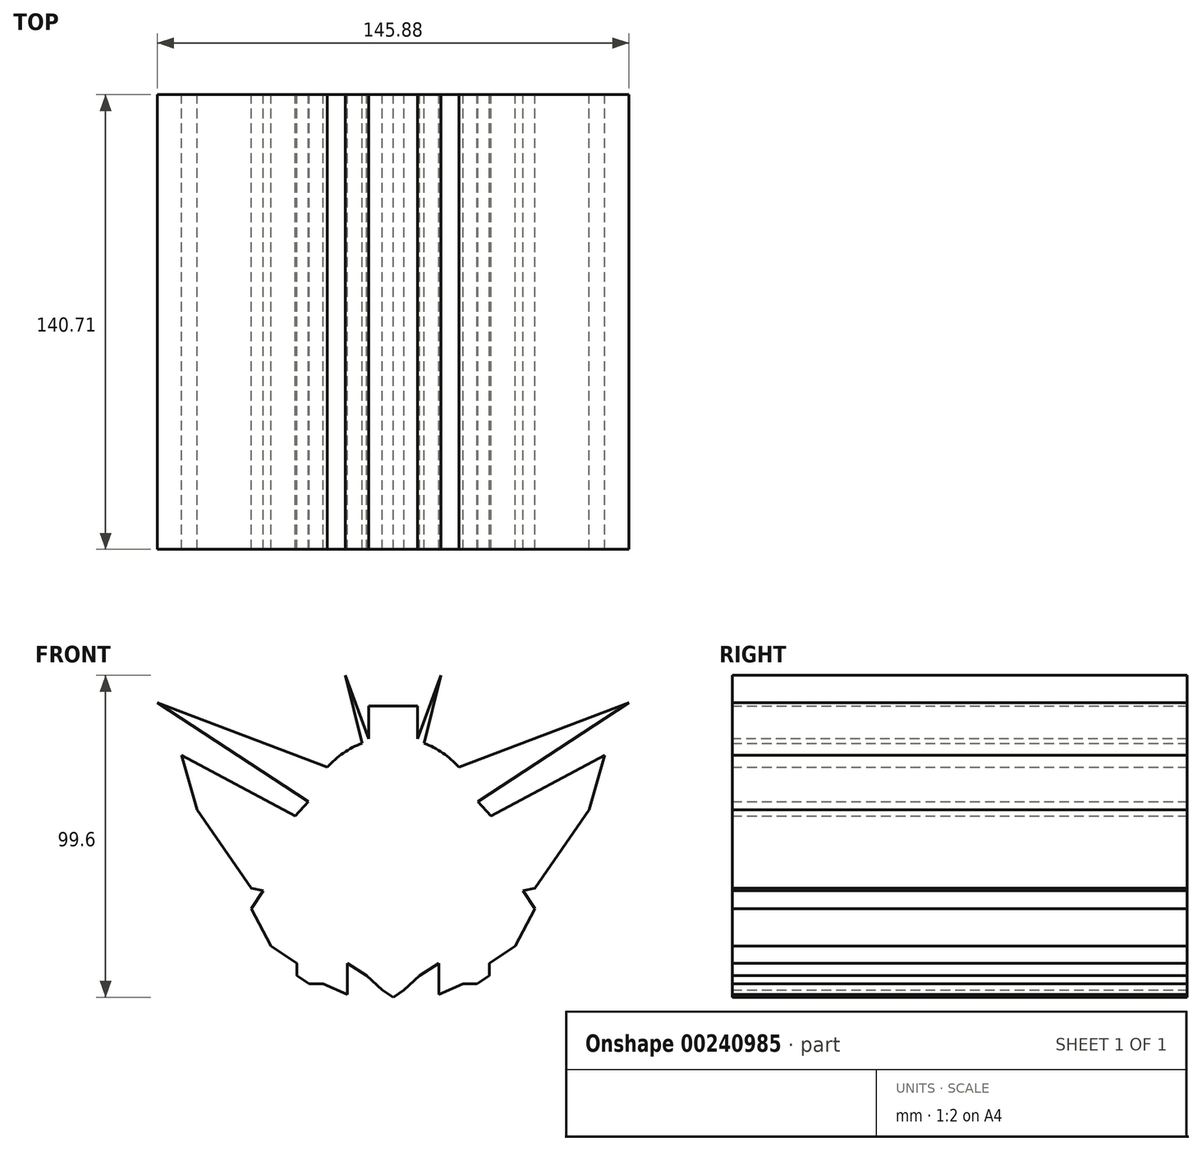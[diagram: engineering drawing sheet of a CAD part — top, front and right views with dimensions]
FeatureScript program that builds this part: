
annotation { "Feature Type Name" : "Feature", "Feature Type Description" : "" }
export const myFeature = defineFeature(function(context is Context, id is Id, definition is map)
    precondition{}
    {
        {
            var Q0;
            Q0=qCreatedBy(makeId("Front.planeOp"),FACE);
            var sketch = newSketch(context, id + "F0", { "sketchPlane" : qUnion([Q0])});
            skCircle(sketch, "E0", {"center": v(0, 16.6) * mm, "radius": 27.21 * mm});
            skPoint(sketch, "E0.first.point", {"position": v(0, 43.81) * mm});
            skPoint(sketch, "E0.second.point", {"position": v(0, -10.61) * mm});
            skPoint(sketch, "E0.third.point", {"position": v(-24.25, 28.94) * mm});
            skLineSegment(sketch, "E1.bottom", {"start": v(-7.19, 53.62) * mm, "end": v(7.51, 53.62) * mm});
            skLineSegment(sketch, "E1.top", {"start": v(-7.19, 11.72) * mm, "end": v(7.51, 11.72) * mm});
            skLineSegment(sketch, "E1.left", {"start": v(-7.19, 53.62) * mm, "end": v(-7.19, 11.72) * mm});
            skLineSegment(sketch, "E1.right", {"start": v(7.51, 53.62) * mm, "end": v(7.51, 11.72) * mm});
            skLineSegment(sketch, "E2", {"start": v(-7.19, 32.67) * mm, "end": v(-14.8, 63.08) * mm});
            skLineSegment(sketch, "E3", {"start": v(-14.8, 63.08) * mm, "end": v(-4.66, 35.7) * mm});
            skLineSegment(sketch, "E4", {"start": v(-4.66, 35.7) * mm, "end": v(-7.19, 32.67) * mm});
            skLineSegment(sketch, "E5", {"start": v(-72.94, 54.63) * mm, "end": v(0, 26.91) * mm});
            skLineSegment(sketch, "E6", {"start": v(0, 26.91) * mm, "end": v(-14.8, 16.6) * mm});
            skLineSegment(sketch, "E7", {"start": v(-14.8, 16.6) * mm, "end": v(-72.94, 54.63) * mm});
            skLineSegment(sketch, "E8", {"start": v(-26.17, 24.04) * mm, "end": v(-43.87, 4.94) * mm});
            skPoint(sketch, "E8.endSnap0", {"position": v(-43.87, 35.62) * mm});
            skLineSegment(sketch, "E9", {"start": v(-43.87, 4.94) * mm, "end": v(-21.56, 11.36) * mm});
            skLineSegment(sketch, "E10", {"start": v(-21.56, 11.36) * mm, "end": v(-26.17, 24.04) * mm});
            skLineSegment(sketch, "E11", {"start": v(-30.34, 19.54) * mm, "end": v(-65.5, 38.4) * mm});
            skLineSegment(sketch, "E12", {"start": v(-65.5, 38.4) * mm, "end": v(-60.62, 21.45) * mm});
            skLineSegment(sketch, "E13", {"start": v(-60.62, 21.45) * mm, "end": v(-43.87, -2.84) * mm});
            skLineSegment(sketch, "E14", {"start": v(-43.87, -2.84) * mm, "end": v(-40.24, -3.52) * mm});
            skLineSegment(sketch, "E15", {"start": v(-40.24, -3.52) * mm, "end": v(-43.87, -9.07) * mm});
            skLineSegment(sketch, "E16", {"start": v(-43.87, -9.07) * mm, "end": v(-37.79, -20.75) * mm});
            skLineSegment(sketch, "E17", {"start": v(-37.79, -20.75) * mm, "end": v(-29.78, -25.99) * mm});
            skLineSegment(sketch, "E18", {"start": v(-29.78, -25.99) * mm, "end": v(-29.78, -29.88) * mm});
            skLineSegment(sketch, "E19", {"start": v(-14.12, -35.62) * mm, "end": v(-14.12, -25.99) * mm});
            skLineSegment(sketch, "E20", {"start": v(-14.12, -25.99) * mm, "end": v(-8.17, -29.88) * mm});
            skLineSegment(sketch, "E21", {"start": v(-8.17, -29.88) * mm, "end": v(-3.42, -34.28) * mm});
            skLineSegment(sketch, "E22", {"start": v(-3.42, -34.28) * mm, "end": v(0, -36.52) * mm});
            skLineSegment(sketch, "E23", {"start": v(0, -36.52) * mm, "end": v(0, -10.61) * mm});
            skLineSegment(sketch, "E24", {"start": v(-29.78, -29.88) * mm, "end": v(-25.94, -32.33) * mm});
            skLineSegment(sketch, "E25", {"start": v(-25.94, -32.33) * mm, "end": v(-21.66, -32.33) * mm});
            skLineSegment(sketch, "E26", {"start": v(-21.66, -32.33) * mm, "end": v(-14.12, -35.62) * mm});
            skSolve(sketch);
        }
        {
            var Q0;
            {var subQ0=sQuery(id+"F0.wireOp",EDGE,"E8");var subQ3=sQuery(id+"F0.wireOp",EDGE,"E9");var subQ6=makeQuery(id+"F0.imprint","INTERSECT",VERTEX,{"derivedFrom":[subQ0,subQ3]});Q0=makeQuery(id+"F0.imprint","IMPRINT",FACE,{"disambiguationData":[TD([[makeQuery(id+"F0.imprint","IMPRINT",EDGE,{"disambiguationData":[TD([[subQ6,1.0]])],"derivedFrom":subQ0}),1.0]])]});}
            var Q1;
            {var subQ0=sQuery(id+"F0.wireOp",EDGE,"E2");var subQ1=sQuery(id+"F0.wireOp",EDGE,"E0");var subQ2=makeQuery(id+"F0.imprint","INTERSECT",VERTEX,{"derivedFrom":[subQ1,subQ0]});Q1=makeQuery(id+"F0.imprint","IMPRINT",FACE,{"disambiguationData":[TD([[makeQuery(id+"F0.imprint","IMPRINT",EDGE,{"disambiguationData":[TD([[subQ2,-1.0]])],"derivedFrom":subQ1}),1.0]])]});}
            var Q2;
            {var subQ0=sQuery(id+"F0.wireOp",EDGE,"E11");Q2=makeQuery(id+"F0.imprint","IMPRINT",FACE,{"disambiguationData":[TD([[makeQuery(id+"F0.imprint","IMPRINT",EDGE,{"derivedFrom":subQ0}),1.0]])]});}
            var Q3;
            {var subQ0=sQuery(id+"F0.wireOp",EDGE,"E5");var subQ1=sQuery(id+"F0.wireOp",EDGE,"E1.left");var subQ2=makeQuery(id+"F0.imprint","INTERSECT",VERTEX,{"derivedFrom":[subQ1,subQ0]});Q3=makeQuery(id+"F0.imprint","IMPRINT",FACE,{"disambiguationData":[TD([[makeQuery(id+"F0.imprint","IMPRINT",EDGE,{"disambiguationData":[TD([[subQ2,-1.0]])],"derivedFrom":subQ1}),1.0]])]});}
            var Q4;
            {var subQ0=sQuery(id+"F0.wireOp",EDGE,"E3");var subQ1=sQuery(id+"F0.wireOp",EDGE,"E0");var subQ2=makeQuery(id+"F0.imprint","INTERSECT",VERTEX,{"derivedFrom":[subQ1,subQ0]});Q4=makeQuery(id+"F0.imprint","IMPRINT",FACE,{"disambiguationData":[TD([[makeQuery(id+"F0.imprint","IMPRINT",EDGE,{"disambiguationData":[TD([[subQ2,-1.0]])],"derivedFrom":subQ1}),1.0]])]});}
            var Q5;
            {var subQ3=sQuery(id+"F0.wireOp",EDGE,"E1.left");var subQ5=sQuery(id+"F0.wireOp",EDGE,"E5");var subQ8=makeQuery(id+"F0.imprint","INTERSECT",VERTEX,{"derivedFrom":[subQ3,subQ5]});Q5=makeQuery(id+"F0.imprint","IMPRINT",FACE,{"disambiguationData":[TD([[makeQuery(id+"F0.imprint","IMPRINT",EDGE,{"disambiguationData":[TD([[subQ8,-1.0]])],"derivedFrom":subQ3}),-1.0]])]});}
            var Q6;
            {var subQ0=sQuery(id+"F0.wireOp",EDGE,"E7");var subQ3=sQuery(id+"F0.wireOp",EDGE,"E5");var subQ5=makeQuery(id+"F0.imprint","INTERSECT",VERTEX,{"derivedFrom":[subQ3,subQ0]});Q6=makeQuery(id+"F0.imprint","IMPRINT",FACE,{"disambiguationData":[TD([[makeQuery(id+"F0.imprint","IMPRINT",EDGE,{"disambiguationData":[TD([[subQ5,-1.0]])],"derivedFrom":subQ3}),-1.0]])]});}
            var Q7;
            {var subQ0=sQuery(id+"F0.wireOp",EDGE,"E10");Q7=makeQuery(id+"F0.imprint","IMPRINT",FACE,{"disambiguationData":[TD([[makeQuery(id+"F0.imprint","IMPRINT",EDGE,{"derivedFrom":subQ0}),1.0]])]});}
            var Q8;
            {var subQ0=sQuery(id+"F0.wireOp",EDGE,"E3");var subQ1=sQuery(id+"F0.wireOp",EDGE,"E0");var subQ2=makeQuery(id+"F0.imprint","INTERSECT",VERTEX,{"derivedFrom":[subQ1,subQ0]});Q8=makeQuery(id+"F0.imprint","IMPRINT",FACE,{"disambiguationData":[TD([[makeQuery(id+"F0.imprint","IMPRINT",EDGE,{"disambiguationData":[TD([[subQ2,-1.0]])],"derivedFrom":subQ1}),-1.0]])]});}
            var Q9;
            {var subQ0=sQuery(id+"F0.wireOp",EDGE,"E4");Q9=makeQuery(id+"F0.imprint","IMPRINT",FACE,{"disambiguationData":[TD([[makeQuery(id+"F0.imprint","IMPRINT",EDGE,{"derivedFrom":subQ0}),-1.0]])]});}
            var Q10;
            {var subQ0=sQuery(id+"F0.wireOp",EDGE,"E1.left");var subQ1=sQuery(id+"F0.wireOp",EDGE,"E0");var subQ2=makeQuery(id+"F0.imprint","INTERSECT",VERTEX,{"derivedFrom":[subQ1,subQ0]});Q10=makeQuery(id+"F0.imprint","IMPRINT",FACE,{"disambiguationData":[TD([[makeQuery(id+"F0.imprint","IMPRINT",EDGE,{"disambiguationData":[TD([[subQ2,-1.0]])],"derivedFrom":subQ1}),1.0]])]});}
            var Q11;
            {var subQ1=sQuery(id+"F0.wireOp",EDGE,"E1.top");Q11=makeQuery(id+"F0.imprint","IMPRINT",FACE,{"disambiguationData":[TD([[makeQuery(id+"F0.imprint","IMPRINT",EDGE,{"derivedFrom":subQ1}),-1.0]])]});}
            var Q12;
            {var subQ11=sQuery(id+"F0.wireOp",EDGE,"E1.top");Q12=makeQuery(id+"F0.imprint","IMPRINT",FACE,{"disambiguationData":[TD([[makeQuery(id+"F0.imprint","IMPRINT",EDGE,{"derivedFrom":subQ11}),1.0]])]});}
            var Q13;
            {var subQ5=sQuery(id+"F0.wireOp",EDGE,"E1.bottom");Q13=makeQuery(id+"F0.imprint","IMPRINT",FACE,{"disambiguationData":[TD([[makeQuery(id+"F0.imprint","IMPRINT",EDGE,{"derivedFrom":subQ5}),-1.0]])]});}
            extrude(context, id + "F1", {"entities" : qUnion([Q0, Q1, Q2, Q3, Q4, Q5, Q6, Q7, Q8, Q9, Q10, Q11, Q12, Q13]), "depth" : 68.07 * mm, "hasSecondDirection" : true, "secondDirectionOppositeDirection" : true, "secondDirectionDepth" : 72.64 * mm});
        }
        {
            var Q0;
            Q0=makeQuery(id+"F1.opExtrude","SWEPT_BODY",BODY,{"disambiguationData":[OSD([sQuery(id+"F0.wireOp",EDGE,"E0"),sQuery(id+"F0.wireOp",EDGE,"E1.bottom"),sQuery(id+"F0.wireOp",EDGE,"E1.left"),sQuery(id+"F0.wireOp",EDGE,"E1.right"),sQuery(id+"F0.wireOp",EDGE,"E2"),sQuery(id+"F0.wireOp",EDGE,"E3"),sQuery(id+"F0.wireOp",EDGE,"E5"),sQuery(id+"F0.wireOp",EDGE,"E7"),sQuery(id+"F0.wireOp",EDGE,"E8"),sQuery(id+"F0.wireOp",EDGE,"E11"),sQuery(id+"F0.wireOp",EDGE,"E12"),sQuery(id+"F0.wireOp",EDGE,"E13"),sQuery(id+"F0.wireOp",EDGE,"E14"),sQuery(id+"F0.wireOp",EDGE,"E15"),sQuery(id+"F0.wireOp",EDGE,"E16"),sQuery(id+"F0.wireOp",EDGE,"E17"),sQuery(id+"F0.wireOp",EDGE,"E18"),sQuery(id+"F0.wireOp",EDGE,"E19"),sQuery(id+"F0.wireOp",EDGE,"E20"),sQuery(id+"F0.wireOp",EDGE,"E21"),sQuery(id+"F0.wireOp",EDGE,"E22"),sQuery(id+"F0.wireOp",EDGE,"E23"),sQuery(id+"F0.wireOp",EDGE,"E24"),sQuery(id+"F0.wireOp",EDGE,"E25"),sQuery(id+"F0.wireOp",EDGE,"E26")])]});
            var Q1;
            Q1=qCreatedBy(makeId("Right.planeOp"),FACE);
            mirror(context, id + "F2", {"operationType" : NewBodyOperationType.ADD, "entities" : qUnion([Q0]), "mirrorPlane" : qUnion([Q1])});
        }
    });
